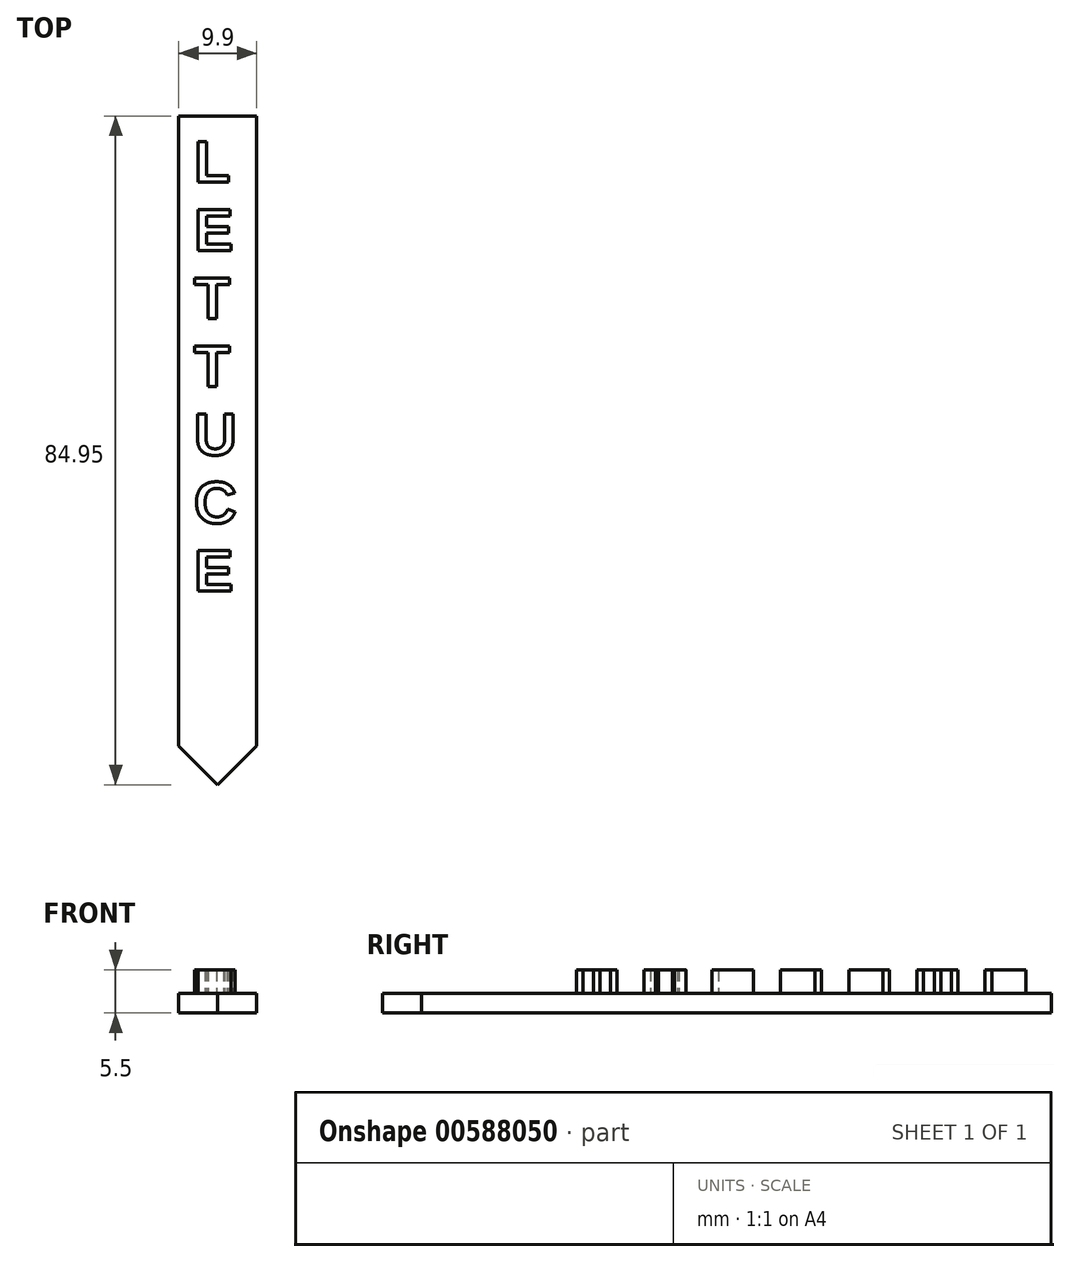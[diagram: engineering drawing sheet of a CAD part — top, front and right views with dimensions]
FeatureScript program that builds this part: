
annotation { "Feature Type Name" : "Feature", "Feature Type Description" : "" }
export const myFeature = defineFeature(function(context is Context, id is Id, definition is map)
    precondition{}
    {
        {
            var Q0;
            Q0=qCreatedBy(makeId("Top.planeOp"),FACE);
            var sketch = newSketch(context, id + "F0", { "sketchPlane" : qUnion([Q0])});
            skLineSegment(sketch, "E0", {"start": v(0, 0) * mm, "end": v(4.95, 4.95) * mm});
            skLineSegment(sketch, "E1", {"start": v(0, 0) * mm, "end": v(-4.95, 4.95) * mm});
            skPoint(sketch, "E2.end.orphan", {"position": v(-3.53, 0) * mm});
            skPoint(sketch, "E3.end.orphan", {"position": v(4.95, 0) * mm});
            skLineSegment(sketch, "E4", {"start": v(4.95, 4.95) * mm, "end": v(4.95, 84.95) * mm});
            skLineSegment(sketch, "E5", {"start": v(-4.95, 4.95) * mm, "end": v(-4.95, 84.95) * mm});
            skLineSegment(sketch, "E6", {"start": v(-4.95, 84.95) * mm, "end": v(4.95, 84.95) * mm});
            skSolve(sketch);
        }
        {
            var Q0;
            Q0=qSketchRegion(id+"F0",true);
            extrude(context, id + "F1", {"entities" : qUnion([Q0]), "depth" : 2.5 * mm, "offsetDistance" : 25 * mm});
        }
        {
            var Q0;
            Q0=makeQuery(id+"F1.opExtrude","CAP_FACE",FACE,{"disambiguationData":[OSD([sQuery(id+"F0.wireOp",EDGE,"E0"),sQuery(id+"F0.wireOp",EDGE,"E1"),sQuery(id+"F0.wireOp",EDGE,"E4"),sQuery(id+"F0.wireOp",EDGE,"E5"),sQuery(id+"F0.wireOp",EDGE,"E6")])],"isStart":false});
            var sketch = newSketch(context, id + "F2", { "sketchPlane" : qUnion([Q0])});
            skText(sketch, "E7", { "text": "L\nE\nT\nT\nU\nC\nE", "fontName": "Arimo-Bold.ttf"});
            const initialGuessF2  = {"E7": [-0.00301, 0.07653, 1, 0, 0.00542]};
            skSetInitialGuess(sketch, initialGuessF2);
            skSolve(sketch);
        }
        {
            var Q0;
            Q0=qSketchRegion(id+"F2",true);
            extrude(context, id + "F3", {"entities" : qUnion([Q0]), "operationType" : NewBodyOperationType.ADD, "depth" : 3 * mm, "offsetDistance" : 25 * mm});
        }
    });
